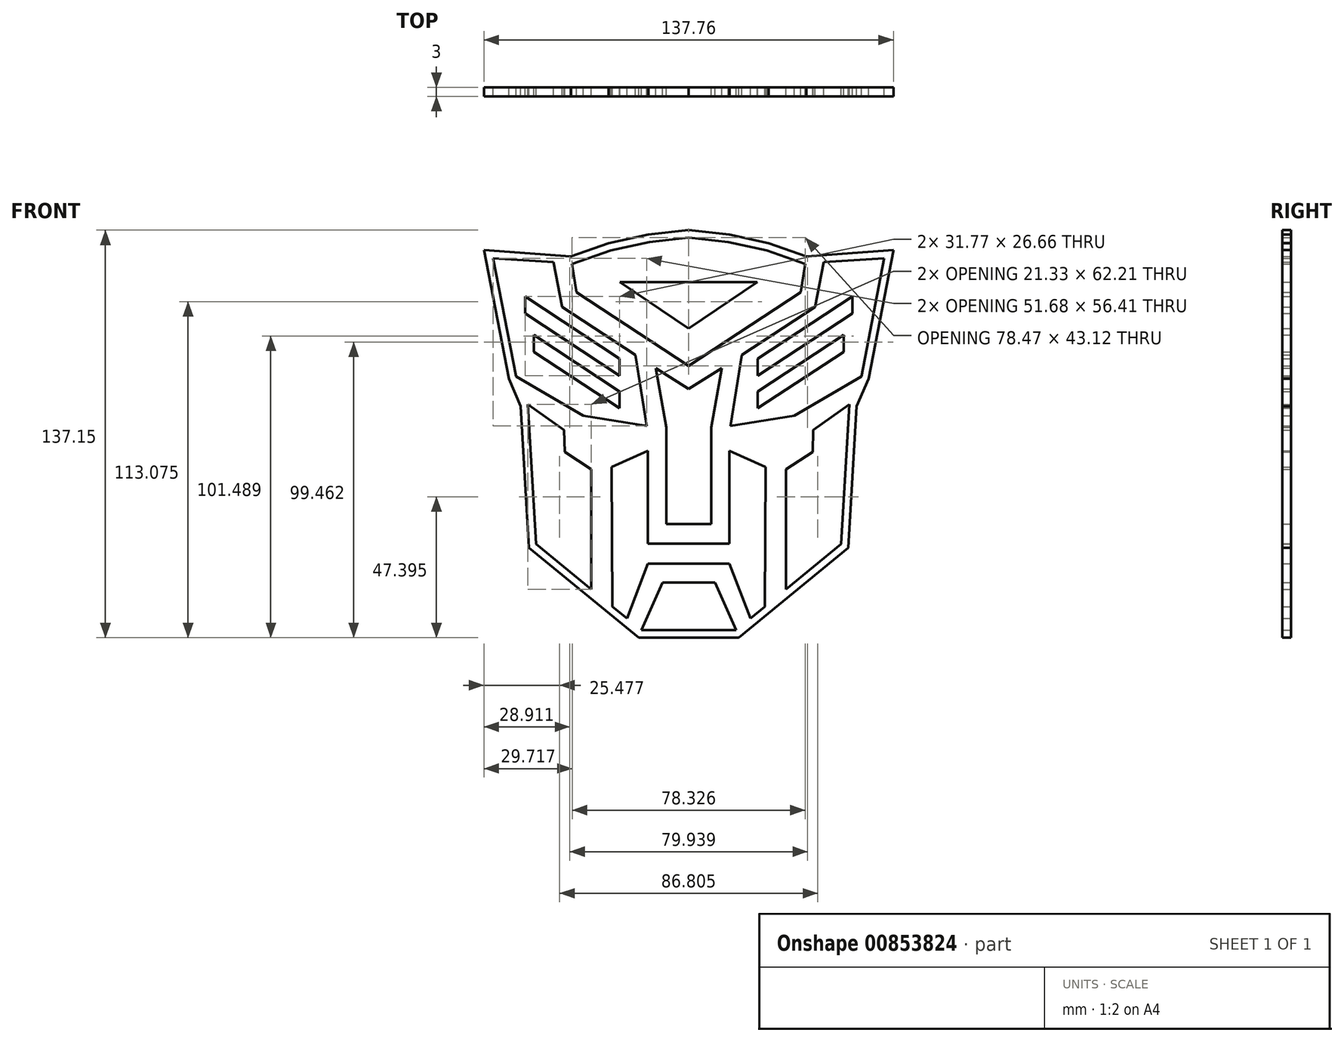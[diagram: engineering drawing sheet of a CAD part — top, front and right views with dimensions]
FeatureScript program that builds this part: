
annotation { "Feature Type Name" : "Feature", "Feature Type Description" : "" }
export const myFeature = defineFeature(function(context is Context, id is Id, definition is map)
    precondition{}
    {
        {
            var Q0;
            Q0=qCreatedBy(makeId("Front.planeOp"),FACE);
            var sketch = newSketch(context, id + "F0", { "sketchPlane" : qUnion([Q0])});
            skLineSegment(sketch, "E0", {"start": v(0, 59.2) * mm, "end": v(-13.27, 57.71) * mm});
            skLineSegment(sketch, "E1", {"start": v(-13.27, 57.71) * mm, "end": v(-26.23, 54.93) * mm});
            skLineSegment(sketch, "E2", {"start": v(-26.23, 54.93) * mm, "end": v(-39.24, 50.35) * mm});
            skLineSegment(sketch, "E3", {"start": v(-65.8, 52.23) * mm, "end": v(-58.11, 12.44) * mm});
            skLineSegment(sketch, "E4", {"start": v(-54.07, 3.06) * mm, "end": v(-51.3, -43.91) * mm});
            skLineSegment(sketch, "E5", {"start": v(-51.3, -43.91) * mm, "end": v(-32.74, -59.15) * mm});
            skLineSegment(sketch, "E6", {"start": v(-15.95, -72.94) * mm, "end": v(0, -72.94) * mm});
            skLineSegment(sketch, "E7.0", {"start": v(-16.84, -75.44) * mm, "end": v(0, -75.44) * mm});
            skLineSegment(sketch, "E7.1", {"start": v(-53.73, -45.15) * mm, "end": v(-16.84, -75.44) * mm});
            skLineSegment(sketch, "E7.2", {"start": v(-56.54, 2.48) * mm, "end": v(-53.73, -45.15) * mm});
            skLineSegment(sketch, "E7.3", {"start": v(-60.52, 11.7) * mm, "end": v(-56.54, 2.48) * mm});
            skLineSegment(sketch, "E7.4", {"start": v(-68.88, 54.95) * mm, "end": v(-60.52, 11.7) * mm});
            skLineSegment(sketch, "E7.5", {"start": v(0, 61.71) * mm, "end": v(-13.67, 60.18) * mm});
            skLineSegment(sketch, "E7.6", {"start": v(-13.67, 60.18) * mm, "end": v(-26.91, 57.34) * mm});
            skLineSegment(sketch, "E7.7", {"start": v(-26.91, 57.34) * mm, "end": v(-39.6, 52.88) * mm});
            skLineSegment(sketch, "E7.8", {"start": v(-39.6, 52.88) * mm, "end": v(-68.88, 54.95) * mm});
            skLineSegment(sketch, "E8", {"start": v(0, 44.24) * mm, "end": v(-23.13, 44.24) * mm});
            skLineSegment(sketch, "E9", {"start": v(-23.13, 44.24) * mm, "end": v(0, 28.63) * mm});
            skLineSegment(sketch, "E10", {"start": v(-39.24, 50.35) * mm, "end": v(-37.75, 40.82) * mm});
            skLineSegment(sketch, "E11", {"start": v(-37.75, 40.82) * mm, "end": v(0, 16.08) * mm});
            skLineSegment(sketch, "E12", {"start": v(-45.46, 50.92) * mm, "end": v(-42.55, 35.86) * mm});
            skLineSegment(sketch, "E13", {"start": v(-42.55, 35.86) * mm, "end": v(-17.9, 19.65) * mm});
            skLineSegment(sketch, "E14", {"start": v(-17.9, 19.65) * mm, "end": v(-14.13, -4.18) * mm});
            skLineSegment(sketch, "E15", {"start": v(-14.13, -4.18) * mm, "end": v(-35.49, -0.69) * mm});
            skLineSegment(sketch, "E16", {"start": v(-35.49, -0.69) * mm, "end": v(-58.11, 12.44) * mm});
            skLineSegment(sketch, "E17", {"start": v(-54.07, 3.06) * mm, "end": v(-41.9, -5.52) * mm});
            skLineSegment(sketch, "E18", {"start": v(-41.9, -5.52) * mm, "end": v(-41.72, -12.9) * mm});
            skLineSegment(sketch, "E19", {"start": v(-41.72, -12.9) * mm, "end": v(-32.74, -18.77) * mm});
            skLineSegment(sketch, "E20", {"start": v(-32.74, -18.77) * mm, "end": v(-32.74, -59.15) * mm});
            skLineSegment(sketch, "E21.trimOffspring", {"start": v(-45.46, 50.92) * mm, "end": v(-65.8, 52.23) * mm});
            skLineSegment(sketch, "E22", {"start": v(-25.63, -64.98) * mm, "end": v(-25.92, -17.97) * mm});
            skLineSegment(sketch, "E23", {"start": v(-25.92, -17.97) * mm, "end": v(-13.73, -12.6) * mm});
            skLineSegment(sketch, "E24", {"start": v(-13.73, -12.6) * mm, "end": v(-13.73, -43.76) * mm});
            skLineSegment(sketch, "E25", {"start": v(-13.73, -43.76) * mm, "end": v(0, -43.76) * mm});
            skLineSegment(sketch, "E26", {"start": v(-20.78, -68.97) * mm, "end": v(-13.73, -50.52) * mm});
            skLineSegment(sketch, "E27", {"start": v(-13.73, -50.52) * mm, "end": v(0, -50.52) * mm});
            skLineSegment(sketch, "E28", {"start": v(-15.95, -72.94) * mm, "end": v(-8.81, -56.88) * mm});
            skLineSegment(sketch, "E29", {"start": v(-8.81, -56.88) * mm, "end": v(0, -56.88) * mm});
            skLineSegment(sketch, "E30.trimOffspring", {"start": v(-25.63, -64.98) * mm, "end": v(-20.78, -68.97) * mm});
            skLineSegment(sketch, "E31", {"start": v(0, 8.34) * mm, "end": v(-11.13, 15.26) * mm});
            skLineSegment(sketch, "E32", {"start": v(-11.13, 15.26) * mm, "end": v(-7.57, -4.73) * mm});
            skLineSegment(sketch, "E33", {"start": v(-7.57, -4.73) * mm, "end": v(-7.57, -37.25) * mm});
            skLineSegment(sketch, "E34", {"start": v(-7.57, -37.25) * mm, "end": v(0, -37.25) * mm});
            skLineSegment(sketch, "E35", {"start": v(-55.05, 39.38) * mm, "end": v(-23.28, 18.47) * mm});
            skLineSegment(sketch, "E36", {"start": v(-23.28, 18.47) * mm, "end": v(-23.28, 12.72) * mm});
            skLineSegment(sketch, "E37", {"start": v(-23.28, 12.72) * mm, "end": v(-55.05, 33.62) * mm});
            skLineSegment(sketch, "E38", {"start": v(-55.05, 33.62) * mm, "end": v(-55.05, 39.38) * mm});
            skLineSegment(sketch, "E39", {"start": v(-52.13, 26.43) * mm, "end": v(-23.28, 7.44) * mm});
            skLineSegment(sketch, "E40", {"start": v(-23.28, 7.44) * mm, "end": v(-23.28, 1.75) * mm});
            skLineSegment(sketch, "E41", {"start": v(-23.28, 1.75) * mm, "end": v(-52.13, 20.74) * mm});
            skLineSegment(sketch, "E42", {"start": v(-52.13, 26.43) * mm, "end": v(-52.13, 20.74) * mm});
            skLineSegment(sketch, "E43", {"start": v(0, 0.38) * mm, "end": v(0, -24.15) * mm, "construction": true});
            skLineSegment(sketch, "E44.MirrorCS", {"start": v(55.05, 33.62) * mm, "end": v(55.05, 39.38) * mm});
            skLineSegment(sketch, "E45.MirrorCS", {"start": v(23.28, 18.47) * mm, "end": v(23.28, 12.72) * mm});
            skLineSegment(sketch, "E46.MirrorCS", {"start": v(52.13, 26.43) * mm, "end": v(52.13, 20.74) * mm});
            skLineSegment(sketch, "E47.MirrorCS", {"start": v(23.28, 7.44) * mm, "end": v(23.28, 1.75) * mm});
            skLineSegment(sketch, "E48.MirrorCS", {"start": v(39.24, 50.35) * mm, "end": v(37.75, 40.82) * mm});
            skLineSegment(sketch, "E49.MirrorCS", {"start": v(17.9, 19.65) * mm, "end": v(14.13, -4.18) * mm});
            skLineSegment(sketch, "E50.MirrorCS", {"start": v(15.95, -72.94) * mm, "end": v(8.81, -56.88) * mm});
            skLineSegment(sketch, "E51.MirrorCS", {"start": v(42.55, 35.86) * mm, "end": v(17.9, 19.65) * mm});
            skLineSegment(sketch, "E52.MirrorCS", {"start": v(0, 59.2) * mm, "end": v(13.27, 57.71) * mm});
            skLineSegment(sketch, "E53.MirrorCS", {"start": v(26.91, 57.34) * mm, "end": v(39.6, 52.88) * mm});
            skLineSegment(sketch, "E54.MirrorCS", {"start": v(25.63, -64.98) * mm, "end": v(25.92, -17.97) * mm});
            skLineSegment(sketch, "E55.MirrorCS", {"start": v(45.46, 50.92) * mm, "end": v(65.8, 52.23) * mm});
            skLineSegment(sketch, "E56.MirrorCS", {"start": v(0, 61.71) * mm, "end": v(13.67, 60.18) * mm});
            skLineSegment(sketch, "E57.MirrorCS", {"start": v(13.67, 60.18) * mm, "end": v(26.91, 57.34) * mm});
            skLineSegment(sketch, "E58.MirrorCS", {"start": v(8.81, -56.88) * mm, "end": v(0, -56.88) * mm});
            skLineSegment(sketch, "E59.MirrorCS", {"start": v(41.9, -5.52) * mm, "end": v(41.72, -12.9) * mm});
            skLineSegment(sketch, "E60.MirrorCS", {"start": v(35.49, -0.69) * mm, "end": v(58.11, 12.44) * mm});
            skLineSegment(sketch, "E61.MirrorCS", {"start": v(25.92, -17.97) * mm, "end": v(13.73, -12.6) * mm});
            skLineSegment(sketch, "E62.MirrorCS", {"start": v(13.27, 57.71) * mm, "end": v(26.23, 54.93) * mm});
            skLineSegment(sketch, "E63.MirrorCS", {"start": v(41.72, -12.9) * mm, "end": v(32.74, -18.77) * mm});
            skLineSegment(sketch, "E64.MirrorCS", {"start": v(26.23, 54.93) * mm, "end": v(39.24, 50.35) * mm});
            skLineSegment(sketch, "E65.MirrorCS", {"start": v(54.07, 3.06) * mm, "end": v(51.3, -43.91) * mm});
            skLineSegment(sketch, "E66.MirrorCS", {"start": v(39.6, 52.88) * mm, "end": v(68.88, 54.95) * mm});
            skLineSegment(sketch, "E67.MirrorCS", {"start": v(7.57, -37.25) * mm, "end": v(0, -37.25) * mm});
            skLineSegment(sketch, "E68.MirrorCS", {"start": v(14.13, -4.18) * mm, "end": v(35.49, -0.69) * mm});
            skLineSegment(sketch, "E69.MirrorCS", {"start": v(51.3, -43.91) * mm, "end": v(32.74, -59.15) * mm});
            skLineSegment(sketch, "E70.MirrorCS", {"start": v(23.13, 44.24) * mm, "end": v(0, 28.63) * mm});
            skLineSegment(sketch, "E71.MirrorCS", {"start": v(54.07, 3.06) * mm, "end": v(41.9, -5.52) * mm});
            skLineSegment(sketch, "E72.MirrorCS", {"start": v(13.73, -50.52) * mm, "end": v(0, -50.52) * mm});
            skLineSegment(sketch, "E73.MirrorCS", {"start": v(45.46, 50.92) * mm, "end": v(42.55, 35.86) * mm});
            skLineSegment(sketch, "E74.MirrorCS", {"start": v(23.28, 12.72) * mm, "end": v(55.05, 33.62) * mm});
            skLineSegment(sketch, "E75.MirrorCS", {"start": v(16.84, -75.44) * mm, "end": v(0, -75.44) * mm});
            skLineSegment(sketch, "E76.MirrorCS", {"start": v(25.63, -64.98) * mm, "end": v(20.78, -68.97) * mm});
            skLineSegment(sketch, "E77.MirrorCS", {"start": v(23.28, 1.75) * mm, "end": v(52.13, 20.74) * mm});
            skLineSegment(sketch, "E78.MirrorCS", {"start": v(65.8, 52.23) * mm, "end": v(58.11, 12.44) * mm});
            skLineSegment(sketch, "E79.MirrorCS", {"start": v(0, 8.34) * mm, "end": v(11.13, 15.26) * mm});
            skLineSegment(sketch, "E80.MirrorCS", {"start": v(13.73, -12.6) * mm, "end": v(13.73, -43.76) * mm});
            skLineSegment(sketch, "E81.MirrorCS", {"start": v(11.13, 15.26) * mm, "end": v(7.57, -4.73) * mm});
            skLineSegment(sketch, "E82.MirrorCS", {"start": v(32.74, -18.77) * mm, "end": v(32.74, -59.15) * mm});
            skLineSegment(sketch, "E83.MirrorCS", {"start": v(37.75, 40.82) * mm, "end": v(0, 16.08) * mm});
            skLineSegment(sketch, "E84.MirrorCS", {"start": v(52.13, 26.43) * mm, "end": v(23.28, 7.44) * mm});
            skLineSegment(sketch, "E85.MirrorCS", {"start": v(15.95, -72.94) * mm, "end": v(0, -72.94) * mm});
            skLineSegment(sketch, "E86.MirrorCS", {"start": v(56.54, 2.48) * mm, "end": v(53.73, -45.15) * mm});
            skLineSegment(sketch, "E87.MirrorCS", {"start": v(0, 44.24) * mm, "end": v(23.13, 44.24) * mm});
            skLineSegment(sketch, "E88.MirrorCS", {"start": v(7.57, -4.73) * mm, "end": v(7.57, -37.25) * mm});
            skLineSegment(sketch, "E89.MirrorCS", {"start": v(53.73, -45.15) * mm, "end": v(16.84, -75.44) * mm});
            skLineSegment(sketch, "E90.MirrorCS", {"start": v(20.78, -68.97) * mm, "end": v(13.73, -50.52) * mm});
            skLineSegment(sketch, "E91.MirrorCS", {"start": v(55.05, 39.38) * mm, "end": v(23.28, 18.47) * mm});
            skLineSegment(sketch, "E92.MirrorCS", {"start": v(68.88, 54.95) * mm, "end": v(60.52, 11.7) * mm});
            skLineSegment(sketch, "E93.MirrorCS", {"start": v(13.73, -43.76) * mm, "end": v(0, -43.76) * mm});
            skLineSegment(sketch, "E94.MirrorCS", {"start": v(60.52, 11.7) * mm, "end": v(56.54, 2.48) * mm});
            skPoint(sketch, "E95.orphan", {"position": v(0.8, 9.61) * mm});
            skPoint(sketch, "E96.orphan", {"position": v(-0.8, 9.61) * mm});
            skPoint(sketch, "E97.orphan", {"position": v(0.66, 29.4) * mm});
            skPoint(sketch, "E98.orphan", {"position": v(-0.66, 29.4) * mm});
            skPoint(sketch, "E99.orphan", {"position": v(0.84, 15.43) * mm});
            skPoint(sketch, "E100.orphan", {"position": v(-0.84, 15.43) * mm});
            skSolve(sketch);
        }
        {
            var Q0;
            Q0=makeQuery(id+"F0.imprint","IMPRINT",FACE,{"disambiguationData":[TD([[makeQuery(id+"F0.imprint","IMPRINT",EDGE,{"derivedFrom":sQuery(id+"F0.wireOp",EDGE,"E0")}),-1.0]])]});
            var Q1;
            Q1=makeQuery(id+"F0.imprint","IMPRINT",FACE,{"disambiguationData":[TD([[makeQuery(id+"F0.imprint","IMPRINT",EDGE,{"derivedFrom":sQuery(id+"F0.wireOp",EDGE,"E4")}),1.0]])]});
            var Q2;
            Q2=makeQuery(id+"F0.imprint","IMPRINT",FACE,{"disambiguationData":[TD([[makeQuery(id+"F0.imprint","IMPRINT",EDGE,{"derivedFrom":sQuery(id+"F0.wireOp",EDGE,"E6")}),1.0]])]});
            var Q3;
            Q3=makeQuery(id+"F0.imprint","IMPRINT",FACE,{"disambiguationData":[TD([[makeQuery(id+"F0.imprint","IMPRINT",EDGE,{"derivedFrom":sQuery(id+"F0.wireOp",EDGE,"E8")}),1.0]])]});
            var Q4;
            Q4=makeQuery(id+"F0.imprint","IMPRINT",FACE,{"disambiguationData":[TD([[makeQuery(id+"F0.imprint","IMPRINT",EDGE,{"derivedFrom":sQuery(id+"F0.wireOp",EDGE,"E22")}),-1.0]])]});
            var Q5;
            Q5=makeQuery(id+"F0.imprint","IMPRINT",FACE,{"disambiguationData":[TD([[makeQuery(id+"F0.imprint","IMPRINT",EDGE,{"derivedFrom":sQuery(id+"F0.wireOp",EDGE,"E31")}),1.0]])]});
            var Q6;
            Q6=makeQuery(id+"F0.imprint","IMPRINT",FACE,{"disambiguationData":[TD([[makeQuery(id+"F0.imprint","IMPRINT",EDGE,{"derivedFrom":sQuery(id+"F0.wireOp",EDGE,"E35")}),-1.0]])]});
            var Q7;
            Q7=makeQuery(id+"F0.imprint","IMPRINT",FACE,{"disambiguationData":[TD([[makeQuery(id+"F0.imprint","IMPRINT",EDGE,{"derivedFrom":sQuery(id+"F0.wireOp",EDGE,"E39")}),-1.0]])]});
            var Q8;
            Q8=makeQuery(id+"F0.imprint","IMPRINT",FACE,{"disambiguationData":[TD([[makeQuery(id+"F0.imprint","IMPRINT",EDGE,{"derivedFrom":sQuery(id+"F0.wireOp",EDGE,"E44.MirrorCS")}),1.0]])]});
            var Q9;
            Q9=makeQuery(id+"F0.imprint","IMPRINT",FACE,{"disambiguationData":[TD([[makeQuery(id+"F0.imprint","IMPRINT",EDGE,{"derivedFrom":sQuery(id+"F0.wireOp",EDGE,"E46.MirrorCS")}),-1.0]])]});
            var Q10;
            Q10=makeQuery(id+"F0.imprint","IMPRINT",FACE,{"disambiguationData":[TD([[makeQuery(id+"F0.imprint","IMPRINT",EDGE,{"derivedFrom":sQuery(id+"F0.wireOp",EDGE,"E59.MirrorCS")}),1.0]])]});
            var Q11;
            Q11=makeQuery(id+"F0.imprint","IMPRINT",FACE,{"disambiguationData":[TD([[makeQuery(id+"F0.imprint","IMPRINT",EDGE,{"derivedFrom":sQuery(id+"F0.wireOp",EDGE,"E0")}),1.0]])]});
            var Q12;
            Q12=makeQuery(id+"F0.imprint","IMPRINT",FACE,{"disambiguationData":[TD([[makeQuery(id+"F0.imprint","IMPRINT",EDGE,{"derivedFrom":sQuery(id+"F0.wireOp",EDGE,"E3")}),1.0]])]});
            var Q13;
            Q13=makeQuery(id+"F0.imprint","IMPRINT",FACE,{"disambiguationData":[TD([[makeQuery(id+"F0.imprint","IMPRINT",EDGE,{"derivedFrom":sQuery(id+"F0.wireOp",EDGE,"E44.MirrorCS")}),-1.0]])]});
            extrude(context, id + "F1", {"entities" : qUnion([Q0, Q1, Q2, Q3, Q4, Q5, Q6, Q7, Q8, Q9, Q10, Q11, Q12, Q13]), "flatOperationType" : FlatOperationType.REMOVE, "depth" : 3 * mm, "offsetDistance" : 25 * mm, "domain" : OperationDomain.MODEL});
        }
        {
            var Q0;
            Q0=makeQuery(id+"F0.imprint","IMPRINT",FACE,{"disambiguationData":[TD([[makeQuery(id+"F0.imprint","IMPRINT",EDGE,{"derivedFrom":sQuery(id+"F0.wireOp",EDGE,"E0")}),1.0]])]});
            var Q1;
            Q1=makeQuery(id+"F0.imprint","IMPRINT",FACE,{"disambiguationData":[TD([[makeQuery(id+"F0.imprint","IMPRINT",EDGE,{"derivedFrom":sQuery(id+"F0.wireOp",EDGE,"E3")}),1.0]])]});
            var Q2;
            Q2=makeQuery(id+"F0.imprint","IMPRINT",FACE,{"disambiguationData":[TD([[makeQuery(id+"F0.imprint","IMPRINT",EDGE,{"derivedFrom":sQuery(id+"F0.wireOp",EDGE,"E44.MirrorCS")}),-1.0]])]});
            var Q3;
            Q3=makeQuery(id+"F0.imprint","IMPRINT",FACE,{"disambiguationData":[TD([[makeQuery(id+"F0.imprint","IMPRINT",EDGE,{"derivedFrom":sQuery(id+"F0.wireOp",EDGE,"E4")}),1.0]])]});
            var Q4;
            Q4=makeQuery(id+"F0.imprint","IMPRINT",FACE,{"disambiguationData":[TD([[makeQuery(id+"F0.imprint","IMPRINT",EDGE,{"derivedFrom":sQuery(id+"F0.wireOp",EDGE,"E22")}),-1.0]])]});
            var Q5;
            Q5=makeQuery(id+"F0.imprint","IMPRINT",FACE,{"disambiguationData":[TD([[makeQuery(id+"F0.imprint","IMPRINT",EDGE,{"derivedFrom":sQuery(id+"F0.wireOp",EDGE,"E31")}),1.0]])]});
            var Q6;
            Q6=makeQuery(id+"F0.imprint","IMPRINT",FACE,{"disambiguationData":[TD([[makeQuery(id+"F0.imprint","IMPRINT",EDGE,{"derivedFrom":sQuery(id+"F0.wireOp",EDGE,"E6")}),1.0]])]});
            var Q7;
            Q7=makeQuery(id+"F0.imprint","IMPRINT",FACE,{"disambiguationData":[TD([[makeQuery(id+"F0.imprint","IMPRINT",EDGE,{"derivedFrom":sQuery(id+"F0.wireOp",EDGE,"E59.MirrorCS")}),1.0]])]});
            extrude(context, id + "F2", {"entities" : qUnion([Q0, Q1, Q2, Q3, Q4, Q5, Q6, Q7]), "flatOperationType" : FlatOperationType.REMOVE, "depth" : 3 * mm, "offsetDistance" : 25 * mm, "domain" : OperationDomain.MODEL});
        }
        {
            var Q0;
            Q0=makeQuery(id+"F2.opExtrude","SWEPT_BODY",BODY,{"disambiguationData":[OSD([sQuery(id+"F0.wireOp",EDGE,"E3"),sQuery(id+"F0.wireOp",EDGE,"E12"),sQuery(id+"F0.wireOp",EDGE,"E13"),sQuery(id+"F0.wireOp",EDGE,"E14"),sQuery(id+"F0.wireOp",EDGE,"E15"),sQuery(id+"F0.wireOp",EDGE,"E16"),sQuery(id+"F0.wireOp",EDGE,"E21.trimOffspring"),sQuery(id+"F0.wireOp",EDGE,"E35"),sQuery(id+"F0.wireOp",EDGE,"E36"),sQuery(id+"F0.wireOp",EDGE,"E37"),sQuery(id+"F0.wireOp",EDGE,"E38"),sQuery(id+"F0.wireOp",EDGE,"E39"),sQuery(id+"F0.wireOp",EDGE,"E40"),sQuery(id+"F0.wireOp",EDGE,"E41"),sQuery(id+"F0.wireOp",EDGE,"E42")])]});
            var Q1;
            Q1=makeQuery(id+"F2.opExtrude","SWEPT_BODY",BODY,{"disambiguationData":[OSD([sQuery(id+"F0.wireOp",EDGE,"E0"),sQuery(id+"F0.wireOp",EDGE,"E1"),sQuery(id+"F0.wireOp",EDGE,"E2"),sQuery(id+"F0.wireOp",EDGE,"E8"),sQuery(id+"F0.wireOp",EDGE,"E9"),sQuery(id+"F0.wireOp",EDGE,"E10"),sQuery(id+"F0.wireOp",EDGE,"E11"),sQuery(id+"F0.wireOp",EDGE,"E48.MirrorCS"),sQuery(id+"F0.wireOp",EDGE,"E52.MirrorCS"),sQuery(id+"F0.wireOp",EDGE,"E62.MirrorCS"),sQuery(id+"F0.wireOp",EDGE,"E64.MirrorCS"),sQuery(id+"F0.wireOp",EDGE,"E70.MirrorCS"),sQuery(id+"F0.wireOp",EDGE,"E83.MirrorCS"),sQuery(id+"F0.wireOp",EDGE,"E87.MirrorCS")])]});
            var Q2;
            Q2=makeQuery(id+"F2.opExtrude","SWEPT_BODY",BODY,{"disambiguationData":[OSD([sQuery(id+"F0.wireOp",EDGE,"E44.MirrorCS"),sQuery(id+"F0.wireOp",EDGE,"E45.MirrorCS"),sQuery(id+"F0.wireOp",EDGE,"E46.MirrorCS"),sQuery(id+"F0.wireOp",EDGE,"E47.MirrorCS"),sQuery(id+"F0.wireOp",EDGE,"E49.MirrorCS"),sQuery(id+"F0.wireOp",EDGE,"E51.MirrorCS"),sQuery(id+"F0.wireOp",EDGE,"E55.MirrorCS"),sQuery(id+"F0.wireOp",EDGE,"E60.MirrorCS"),sQuery(id+"F0.wireOp",EDGE,"E68.MirrorCS"),sQuery(id+"F0.wireOp",EDGE,"E73.MirrorCS"),sQuery(id+"F0.wireOp",EDGE,"E74.MirrorCS"),sQuery(id+"F0.wireOp",EDGE,"E77.MirrorCS"),sQuery(id+"F0.wireOp",EDGE,"E78.MirrorCS"),sQuery(id+"F0.wireOp",EDGE,"E84.MirrorCS"),sQuery(id+"F0.wireOp",EDGE,"E91.MirrorCS")])]});
            var Q3;
            Q3=makeQuery(id+"F2.opExtrude","SWEPT_BODY",BODY,{"disambiguationData":[OSD([sQuery(id+"F0.wireOp",EDGE,"E31"),sQuery(id+"F0.wireOp",EDGE,"E32"),sQuery(id+"F0.wireOp",EDGE,"E33"),sQuery(id+"F0.wireOp",EDGE,"E34"),sQuery(id+"F0.wireOp",EDGE,"E67.MirrorCS"),sQuery(id+"F0.wireOp",EDGE,"E79.MirrorCS"),sQuery(id+"F0.wireOp",EDGE,"E81.MirrorCS"),sQuery(id+"F0.wireOp",EDGE,"E88.MirrorCS")])]});
            var Q4;
            Q4=makeQuery(id+"F2.opExtrude","SWEPT_BODY",BODY,{"disambiguationData":[OSD([sQuery(id+"F0.wireOp",EDGE,"E4"),sQuery(id+"F0.wireOp",EDGE,"E5"),sQuery(id+"F0.wireOp",EDGE,"E17"),sQuery(id+"F0.wireOp",EDGE,"E18"),sQuery(id+"F0.wireOp",EDGE,"E19"),sQuery(id+"F0.wireOp",EDGE,"E20")])]});
            var Q5;
            Q5=makeQuery(id+"F2.opExtrude","SWEPT_BODY",BODY,{"disambiguationData":[OSD([sQuery(id+"F0.wireOp",EDGE,"E22"),sQuery(id+"F0.wireOp",EDGE,"E23"),sQuery(id+"F0.wireOp",EDGE,"E24"),sQuery(id+"F0.wireOp",EDGE,"E25"),sQuery(id+"F0.wireOp",EDGE,"E26"),sQuery(id+"F0.wireOp",EDGE,"E27"),sQuery(id+"F0.wireOp",EDGE,"E30.trimOffspring"),sQuery(id+"F0.wireOp",EDGE,"E54.MirrorCS"),sQuery(id+"F0.wireOp",EDGE,"E61.MirrorCS"),sQuery(id+"F0.wireOp",EDGE,"E72.MirrorCS"),sQuery(id+"F0.wireOp",EDGE,"E76.MirrorCS"),sQuery(id+"F0.wireOp",EDGE,"E80.MirrorCS"),sQuery(id+"F0.wireOp",EDGE,"E90.MirrorCS"),sQuery(id+"F0.wireOp",EDGE,"E93.MirrorCS")])]});
            var Q6;
            Q6=makeQuery(id+"F2.opExtrude","SWEPT_BODY",BODY,{"disambiguationData":[OSD([sQuery(id+"F0.wireOp",EDGE,"E6"),sQuery(id+"F0.wireOp",EDGE,"E28"),sQuery(id+"F0.wireOp",EDGE,"E29"),sQuery(id+"F0.wireOp",EDGE,"E50.MirrorCS"),sQuery(id+"F0.wireOp",EDGE,"E58.MirrorCS"),sQuery(id+"F0.wireOp",EDGE,"E85.MirrorCS")])]});
            var Q7;
            Q7=makeQuery(id+"F2.opExtrude","SWEPT_BODY",BODY,{"disambiguationData":[OSD([sQuery(id+"F0.wireOp",EDGE,"E59.MirrorCS"),sQuery(id+"F0.wireOp",EDGE,"E63.MirrorCS"),sQuery(id+"F0.wireOp",EDGE,"E65.MirrorCS"),sQuery(id+"F0.wireOp",EDGE,"E69.MirrorCS"),sQuery(id+"F0.wireOp",EDGE,"E71.MirrorCS"),sQuery(id+"F0.wireOp",EDGE,"E82.MirrorCS")])]});
            var Q8;
            Q8=makeQuery(id+"F1.opExtrude","SWEPT_BODY",BODY,{"disambiguationData":[OSD([sQuery(id+"F0.wireOp",EDGE,"E7.0"),sQuery(id+"F0.wireOp",EDGE,"E7.1"),sQuery(id+"F0.wireOp",EDGE,"E7.2"),sQuery(id+"F0.wireOp",EDGE,"E7.3"),sQuery(id+"F0.wireOp",EDGE,"E7.4"),sQuery(id+"F0.wireOp",EDGE,"E7.5"),sQuery(id+"F0.wireOp",EDGE,"E7.6"),sQuery(id+"F0.wireOp",EDGE,"E7.7"),sQuery(id+"F0.wireOp",EDGE,"E7.8"),sQuery(id+"F0.wireOp",EDGE,"E53.MirrorCS"),sQuery(id+"F0.wireOp",EDGE,"E56.MirrorCS"),sQuery(id+"F0.wireOp",EDGE,"E57.MirrorCS"),sQuery(id+"F0.wireOp",EDGE,"E66.MirrorCS"),sQuery(id+"F0.wireOp",EDGE,"E75.MirrorCS"),sQuery(id+"F0.wireOp",EDGE,"E86.MirrorCS"),sQuery(id+"F0.wireOp",EDGE,"E89.MirrorCS"),sQuery(id+"F0.wireOp",EDGE,"E92.MirrorCS"),sQuery(id+"F0.wireOp",EDGE,"E94.MirrorCS")])]});
            booleanBodies(context, id + "F3", {"operationType" : BooleanOperationType.SUBTRACTION, "tools" : qUnion([Q0, Q1, Q2, Q3, Q4, Q5, Q6, Q7]), "targets" : qUnion([Q8]), "keepTools" : true});
        }
    });
